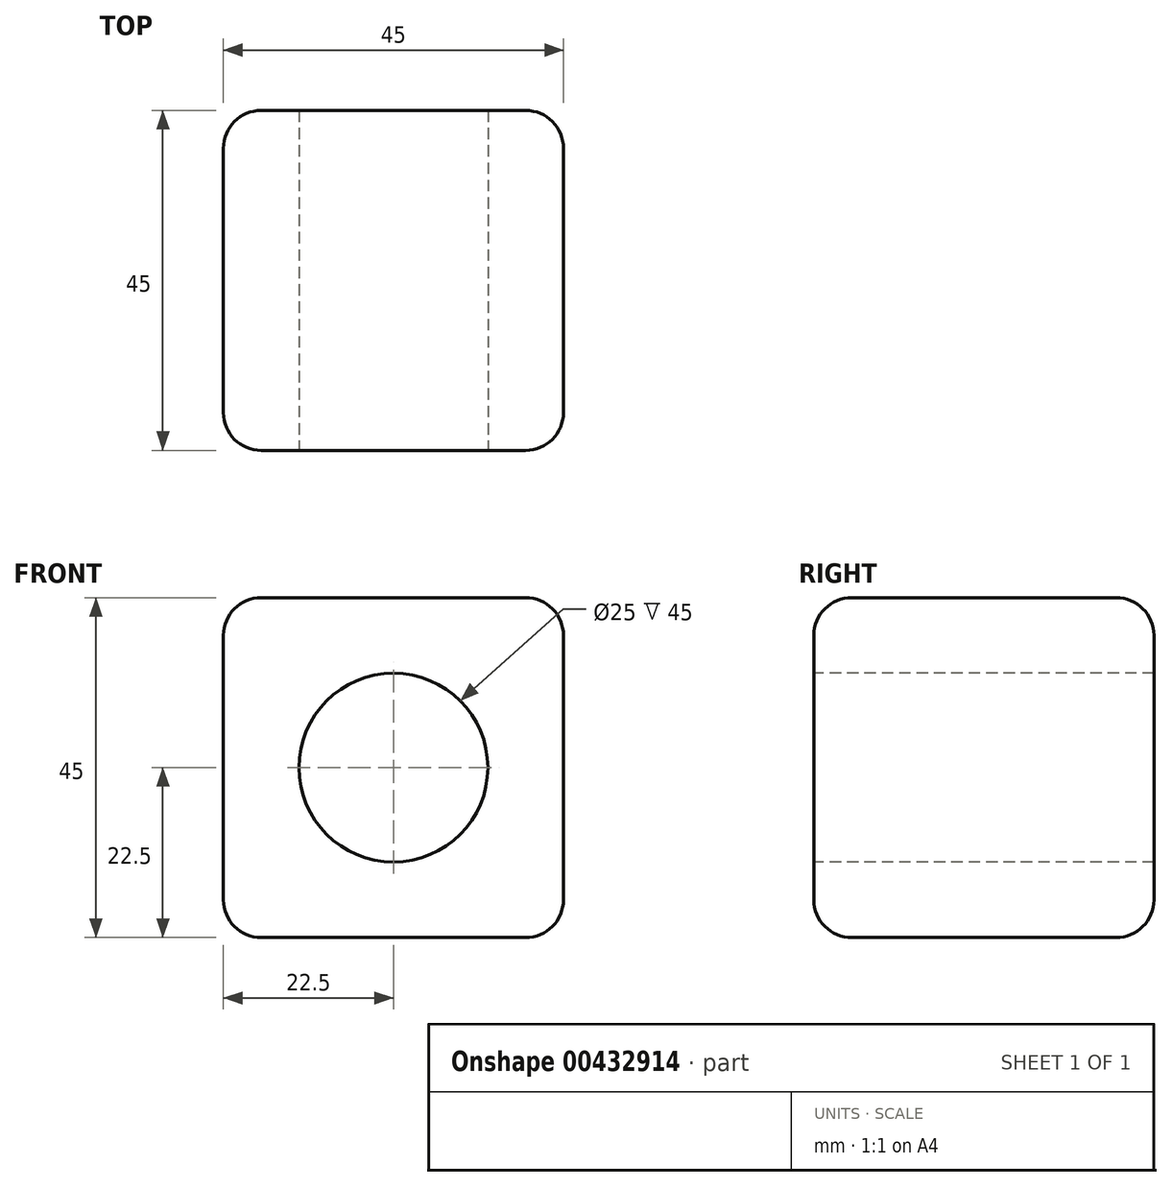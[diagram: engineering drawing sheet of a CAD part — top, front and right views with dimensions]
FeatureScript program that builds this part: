
annotation { "Feature Type Name" : "Feature", "Feature Type Description" : "" }
export const myFeature = defineFeature(function(context is Context, id is Id, definition is map)
    precondition{}
    {
        {
            var Q0;
            Q0=qCreatedBy(makeId("Front.planeOp"),FACE);
            var sketch = newSketch(context, id + "F0", { "sketchPlane" : qUnion([Q0])});
            skLineSegment(sketch, "E0.bottom", {"start": v(0, 0) * mm, "end": v(-45, 0) * mm});
            skLineSegment(sketch, "E0.top", {"start": v(0, 45) * mm, "end": v(-45, 45) * mm});
            skLineSegment(sketch, "E0.left", {"start": v(0, 0) * mm, "end": v(0, 45) * mm});
            skLineSegment(sketch, "E0.right", {"start": v(-45, 0) * mm, "end": v(-45, 45) * mm});
            skSolve(sketch);
        }
        {
            var Q0;
            Q0 = qSketchRegion(id + "F0", true);
            extrude(context, id + "F1", {"entities" : qUnion([Q0]), "depth" : 45 * mm});
        }
        {
            var Q0;
            Q0=makeQuery(id+"F1.opExtrude","CAP_FACE",FACE,{"disambiguationData":[OSD([sQuery(id+"F0.wireOp",EDGE,"E0.bottom"),sQuery(id+"F0.wireOp",EDGE,"E0.top"),sQuery(id+"F0.wireOp",EDGE,"E0.left"),sQuery(id+"F0.wireOp",EDGE,"E0.right")])],"isStart":false});
            var Q1;
            Q1=makeQuery(id+"F1.opExtrude","SWEPT_FACE",FACE,{"disambiguationData":[OSD([sQuery(id+"F0.wireOp",EDGE,"E0.right")])]});
            var Q2;
            Q2=makeQuery(id+"F1.opExtrude","SWEPT_FACE",FACE,{"disambiguationData":[OSD([sQuery(id+"F0.wireOp",EDGE,"E0.top")])]});
            var Q3;
            Q3=makeQuery(id+"F1.opExtrude","SWEPT_FACE",FACE,{"disambiguationData":[OSD([sQuery(id+"F0.wireOp",EDGE,"E0.left")])]});
            var Q4;
            Q4=makeQuery(id+"F1.opExtrude","CAP_FACE",FACE,{"disambiguationData":[OSD([sQuery(id+"F0.wireOp",EDGE,"E0.bottom"),sQuery(id+"F0.wireOp",EDGE,"E0.top"),sQuery(id+"F0.wireOp",EDGE,"E0.left"),sQuery(id+"F0.wireOp",EDGE,"E0.right")])],"isStart":true});
            fillet(context, id + "F2", {"entities" : qUnion([Q0, Q1, Q2, Q3, Q4]), "radius" : 5 * mm, "tangentPropagation" : true, "allowEdgeOverflow" : false});
        }
        {
            var Q0;
            Q0=makeQuery(id+"F1.opExtrude","CAP_FACE",FACE,{"disambiguationData":[OSD([sQuery(id+"F0.wireOp",EDGE,"E0.bottom"),sQuery(id+"F0.wireOp",EDGE,"E0.top"),sQuery(id+"F0.wireOp",EDGE,"E0.left"),sQuery(id+"F0.wireOp",EDGE,"E0.right")])],"isStart":false});
            var sketch = newSketch(context, id + "F3", { "sketchPlane" : qUnion([Q0])});
            skCircle(sketch, "E1", {"center": v(-22.5, 22.5) * mm, "radius": 12.5 * mm});
            skSolve(sketch);
        }
        {
            var Q0;
            Q0=makeQuery(id+"F3.imprint","IMPRINT",FACE,{"disambiguationData":[TD([[makeQuery(id+"F3.imprint","IMPRINT",EDGE,{"derivedFrom":sQuery(id+"F3.wireOp",EDGE,"E1")}),1.0]])]});
            extrude(context, id + "F4", {"entities" : qUnion([Q0]), "operationType" : NewBodyOperationType.REMOVE, "oppositeDirection" : true, "depth" : 45 * mm});
        }
    });
